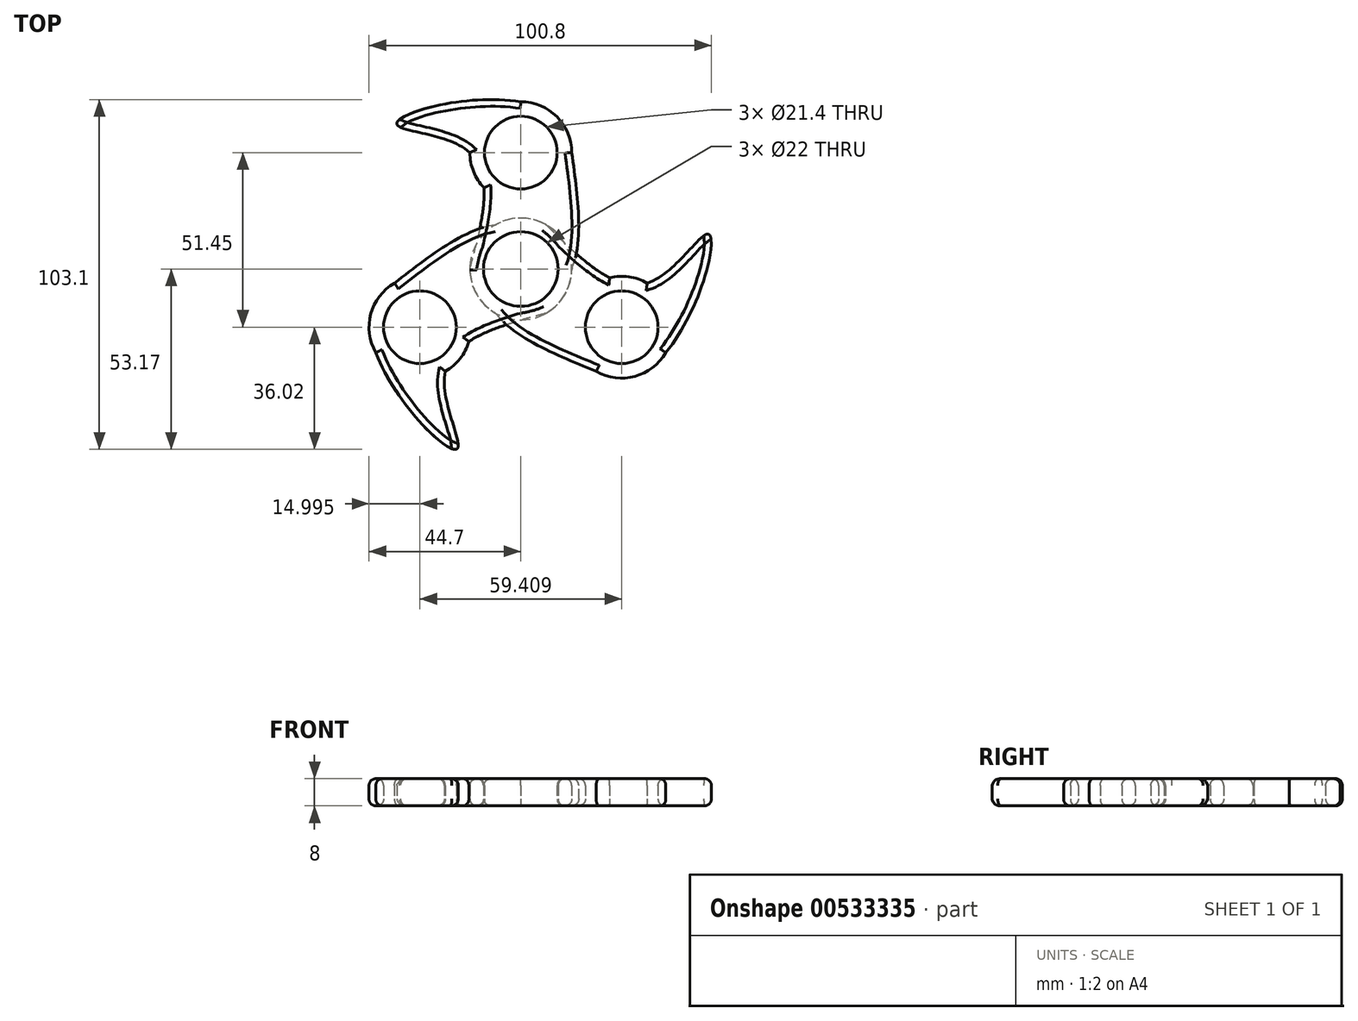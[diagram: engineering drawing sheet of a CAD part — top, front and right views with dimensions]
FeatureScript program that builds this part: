
annotation { "Feature Type Name" : "Feature", "Feature Type Description" : "" }
export const myFeature = defineFeature(function(context is Context, id is Id, definition is map)
    precondition{}
    {
        {
            var Q0;
            Q0=qCreatedBy(makeId("Top.planeOp"),FACE);
            var sketch = newSketch(context, id + "F0", { "sketchPlane" : qUnion([Q0])});
            skCircle(sketch, "E0", {"center": v(0, 0) * mm, "radius": 11 * mm});
            skCircle(sketch, "E1", {"center": v(0, 0) * mm, "radius": 15 * mm});
            skCircle(sketch, "E2", {"center": v(0, 34.3) * mm, "radius": 10.7 * mm});
            skCircle(sketch, "E3", {"center": v(0, 34.3) * mm, "radius": 15 * mm});
            skFitSpline(sketch, "E4", {"points": [v(0, 49.3) * mm, v(-36.48, 42.6) * mm, v(-15, 34.3) * mm, v(-15, 0) * mm], "startDerivative": vector(-141.58, 21.82) * mm, "endDerivative": vector(-27, -103.96) * mm});
            skFitSpline(sketch, "E5", {"points": [v(15, 34.3) * mm, v(15, 0) * mm, v(0, -15) * mm], "startDerivative": vector(9.54, -68.89) * mm, "endDerivative": vector(-41.57, -28.09) * mm});
            skSolve(sketch);
        }
        {
            var Q0;
            {var subQ0=sQuery(id+"F0.wireOp",EDGE,"E4");var subQ1=sQuery(id+"F0.wireOp",EDGE,"E3");var subQ2=makeQuery(id+"F0.imprint","INTERSECT",VERTEX,{"disambiguationData":[OD(0.0)],"derivedFrom":[subQ1,subQ0]});Q0=makeQuery(id+"F0.imprint","IMPRINT",FACE,{"disambiguationData":[TD([[makeQuery(id+"F0.imprint","IMPRINT",EDGE,{"disambiguationData":[TD([[subQ2,-1.0]])],"derivedFrom":subQ1}),-1.0]])]});}
            var Q1;
            Q1=makeQuery(id+"F0.imprint","IMPRINT",FACE,{"disambiguationData":[TD([[makeQuery(id+"F0.imprint","IMPRINT",EDGE,{"derivedFrom":sQuery(id+"F0.wireOp",EDGE,"E2")}),-1.0]])]});
            var Q2;
            {var subQ0=sQuery(id+"F0.wireOp",EDGE,"E4");var subQ1=sQuery(id+"F0.wireOp",EDGE,"E3");var subQ2=makeQuery(id+"F0.imprint","INTERSECT",VERTEX,{"disambiguationData":[OD(1.0)],"derivedFrom":[subQ1,subQ0]});Q2=makeQuery(id+"F0.imprint","IMPRINT",FACE,{"disambiguationData":[TD([[makeQuery(id+"F0.imprint","IMPRINT",EDGE,{"disambiguationData":[TD([[subQ2,-1.0]])],"derivedFrom":subQ1}),1.0]])]});}
            var Q3;
            {var subQ0=sQuery(id+"F0.wireOp",EDGE,"E4");var subQ1=sQuery(id+"F0.wireOp",EDGE,"E1");var subQ2=makeQuery(id+"F0.imprint","INTERSECT",VERTEX,{"disambiguationData":[OD(1.0)],"derivedFrom":[subQ1,subQ0]});Q3=makeQuery(id+"F0.imprint","IMPRINT",FACE,{"disambiguationData":[TD([[makeQuery(id+"F0.imprint","IMPRINT",EDGE,{"disambiguationData":[TD([[subQ2,1.0]])],"derivedFrom":subQ1}),-1.0]])]});}
            var Q4;
            Q4=makeQuery(id+"F0.imprint","IMPRINT",FACE,{"disambiguationData":[TD([[makeQuery(id+"F0.imprint","IMPRINT",EDGE,{"derivedFrom":sQuery(id+"F0.wireOp",EDGE,"E0")}),-1.0]])]});
            var Q5;
            {var subQ0=sQuery(id+"F0.wireOp",EDGE,"E5");var subQ1=sQuery(id+"F0.wireOp",EDGE,"E1");var subQ2=makeQuery(id+"F0.imprint","INTERSECT",VERTEX,{"disambiguationData":[OD(0.0)],"derivedFrom":[subQ1,subQ0]});Q5=makeQuery(id+"F0.imprint","IMPRINT",FACE,{"disambiguationData":[TD([[makeQuery(id+"F0.imprint","IMPRINT",EDGE,{"disambiguationData":[TD([[subQ2,-1.0]])],"derivedFrom":subQ1}),1.0]])]});}
            extrude(context, id + "F1", {"entities" : qUnion([Q0, Q1, Q2, Q3, Q4, Q5]), "depth" : 8 * mm, "offsetDistance" : 25 * mm});
        }
        {
            var Q0;
            {var subQ0=sQuery(id+"F0.wireOp",EDGE,"E4");var subQ1=sQuery(id+"F0.wireOp",EDGE,"E1");var subQ2=makeQuery(id+"F0.imprint","INTERSECT",VERTEX,{"disambiguationData":[OD(1.0)],"derivedFrom":[subQ1,subQ0]});Q0=makeQuery(id+"F1.opExtrude","CAP_EDGE",EDGE,{"disambiguationData":[OSD([subQ0]),TDD([makeQuery(id+"F0.imprint","IMPRINT",EDGE,{"disambiguationData":[TD([[subQ2,1.0]])],"derivedFrom":subQ0}),makeQuery(id+"F0.imprint","IMPRINT",EDGE,{"disambiguationData":[TD([[makeQuery(id+"F0.imprint","INTERSECT",VERTEX,{"disambiguationData":[OD(0.0)],"derivedFrom":[subQ1,subQ0]}),1.0]])],"derivedFrom":subQ0})])],"isStart":false});}
            var Q1;
            {var subQ0=sQuery(id+"F0.wireOp",EDGE,"E4");var subQ1=sQuery(id+"F0.wireOp",EDGE,"E1");var subQ2=makeQuery(id+"F0.imprint","INTERSECT",VERTEX,{"disambiguationData":[OD(1.0)],"derivedFrom":[subQ1,subQ0]});Q1=makeQuery(id+"F1.opExtrude","CAP_EDGE",EDGE,{"disambiguationData":[OSD([subQ0]),TDD([makeQuery(id+"F0.imprint","IMPRINT",EDGE,{"disambiguationData":[TD([[subQ2,1.0]])],"derivedFrom":subQ0}),makeQuery(id+"F0.imprint","IMPRINT",EDGE,{"disambiguationData":[TD([[makeQuery(id+"F0.imprint","INTERSECT",VERTEX,{"disambiguationData":[OD(0.0)],"derivedFrom":[subQ1,subQ0]}),1.0]])],"derivedFrom":subQ0})])],"isStart":true});}
            var Q2;
            {var subQ0=sQuery(id+"F0.wireOp",EDGE,"E4");var subQ1=sQuery(id+"F0.wireOp",EDGE,"E3");Q2=makeQuery(id+"F1.opExtrude","CAP_EDGE",EDGE,{"disambiguationData":[OSD([subQ0]),TDD([makeQuery(id+"F0.imprint","IMPRINT",EDGE,{"disambiguationData":[TD([[makeQuery(id+"F0.imprint","INTERSECT",VERTEX,{"disambiguationData":[OD(0.0)],"derivedFrom":[subQ1,subQ0]}),-1.0]])],"derivedFrom":subQ0})])],"isStart":false});}
            var Q3;
            {var subQ0=sQuery(id+"F0.wireOp",EDGE,"E4");var subQ1=sQuery(id+"F0.wireOp",EDGE,"E3");Q3=makeQuery(id+"F1.opExtrude","CAP_EDGE",EDGE,{"disambiguationData":[OSD([subQ0]),TDD([makeQuery(id+"F0.imprint","IMPRINT",EDGE,{"disambiguationData":[TD([[makeQuery(id+"F0.imprint","INTERSECT",VERTEX,{"disambiguationData":[OD(0.0)],"derivedFrom":[subQ1,subQ0]}),-1.0]])],"derivedFrom":subQ0})])],"isStart":true});}
            var Q4;
            {var subQ0=sQuery(id+"F0.wireOp",EDGE,"E4");var subQ1=sQuery(id+"F0.wireOp",EDGE,"E3");Q4=makeQuery(id+"F1.opExtrude","CAP_EDGE",EDGE,{"disambiguationData":[OSD([subQ1]),TDD([makeQuery(id+"F0.imprint","IMPRINT",EDGE,{"disambiguationData":[TD([[makeQuery(id+"F0.imprint","INTERSECT",VERTEX,{"disambiguationData":[OD(1.0)],"derivedFrom":[subQ1,subQ0]}),-1.0]])],"derivedFrom":subQ1})])],"isStart":false});}
            var Q5;
            {var subQ0=sQuery(id+"F0.wireOp",EDGE,"E4");var subQ1=sQuery(id+"F0.wireOp",EDGE,"E3");Q5=makeQuery(id+"F1.opExtrude","CAP_EDGE",EDGE,{"disambiguationData":[OSD([subQ1]),TDD([makeQuery(id+"F0.imprint","IMPRINT",EDGE,{"disambiguationData":[TD([[makeQuery(id+"F0.imprint","INTERSECT",VERTEX,{"disambiguationData":[OD(1.0)],"derivedFrom":[subQ1,subQ0]}),-1.0]])],"derivedFrom":subQ1})])],"isStart":true});}
            var Q6;
            Q6=makeQuery(id+"F1.opExtrude","CAP_EDGE",EDGE,{"disambiguationData":[OSD([sQuery(id+"F0.wireOp",EDGE,"E0")])],"isStart":false});
            var Q7;
            Q7=makeQuery(id+"F1.opExtrude","SWEPT_FACE",FACE,{"disambiguationData":[OSD([sQuery(id+"F0.wireOp",EDGE,"E1")])]});
            var Q8;
            Q8=makeQuery(id+"F1.opExtrude","CAP_EDGE",EDGE,{"disambiguationData":[OSD([sQuery(id+"F0.wireOp",EDGE,"E5")])],"isStart":false});
            var Q9;
            {var subQ0=sQuery(id+"F0.wireOp",EDGE,"E3");Q9=makeQuery(id+"F1.opExtrude","CAP_EDGE",EDGE,{"disambiguationData":[OSD([subQ0]),TDD([makeQuery(id+"F0.imprint","IMPRINT",EDGE,{"disambiguationData":[TD([[makeQuery(id+"F0.imprint","INTERSECT",VERTEX,{"disambiguationData":[OD(0.0)],"derivedFrom":[subQ0,sQuery(id+"F0.wireOp",EDGE,"E4")]}),1.0]])],"derivedFrom":subQ0})])],"isStart":false});}
            var Q10;
            Q10=makeQuery(id+"F1.opExtrude","CAP_EDGE",EDGE,{"disambiguationData":[OSD([sQuery(id+"F0.wireOp",EDGE,"E5")])],"isStart":true});
            var Q11;
            Q11=makeQuery(id+"F1.opExtrude","CAP_FACE",FACE,{"disambiguationData":[OSD([sQuery(id+"F0.wireOp",EDGE,"E0"),sQuery(id+"F0.wireOp",EDGE,"E1"),sQuery(id+"F0.wireOp",EDGE,"E2"),sQuery(id+"F0.wireOp",EDGE,"E3"),sQuery(id+"F0.wireOp",EDGE,"E4"),sQuery(id+"F0.wireOp",EDGE,"E5")])],"isStart":true});
            var Q12;
            Q12=makeQuery(id+"F1.opExtrude","CAP_EDGE",EDGE,{"disambiguationData":[OSD([sQuery(id+"F0.wireOp",EDGE,"E2")])],"isStart":false});
            fillet(context, id + "F2", {"entities" : qUnion([Q0, Q1, Q2, Q3, Q4, Q5, Q6, Q7, Q8, Q9, Q10, Q11, Q12]), "radius" : 2 * mm, "allowEdgeOverflow" : false});
        }
        {
            var Q0;
            Q0=makeQuery(id+"F1.opExtrude","SWEPT_BODY",BODY,{"disambiguationData":[OSD([sQuery(id+"F0.wireOp",EDGE,"E0"),sQuery(id+"F0.wireOp",EDGE,"E1"),sQuery(id+"F0.wireOp",EDGE,"E2"),sQuery(id+"F0.wireOp",EDGE,"E3"),sQuery(id+"F0.wireOp",EDGE,"E4"),sQuery(id+"F0.wireOp",EDGE,"E5")])]});
            var Q1;
            {var subQ0=sQuery(id+"F0.wireOp",EDGE,"E0");Q1=makeQuery(id+"F2.opFillet","BLEND_EDGE",EDGE,{"blendedFrom":[makeQuery(id+"F1.opExtrude","CAP_EDGE",EDGE,{"disambiguationData":[OSD([subQ0])],"isStart":false}),makeQuery(id+"F1.opExtrude","SWEPT_FACE",FACE,{"disambiguationData":[OSD([subQ0])]})],"blendedInto":[makeQuery(id+"F1.opExtrude","SWEPT_FACE",FACE,{"disambiguationData":[OSD([subQ0])]})]});}
            circularPattern(context, id + "F3", {"entities" : qUnion([Q0]), "axis" : qUnion([Q1]), "angle" : 360 * degree, "instanceCount" : 3, "equalSpace" : true});
        }
    });
